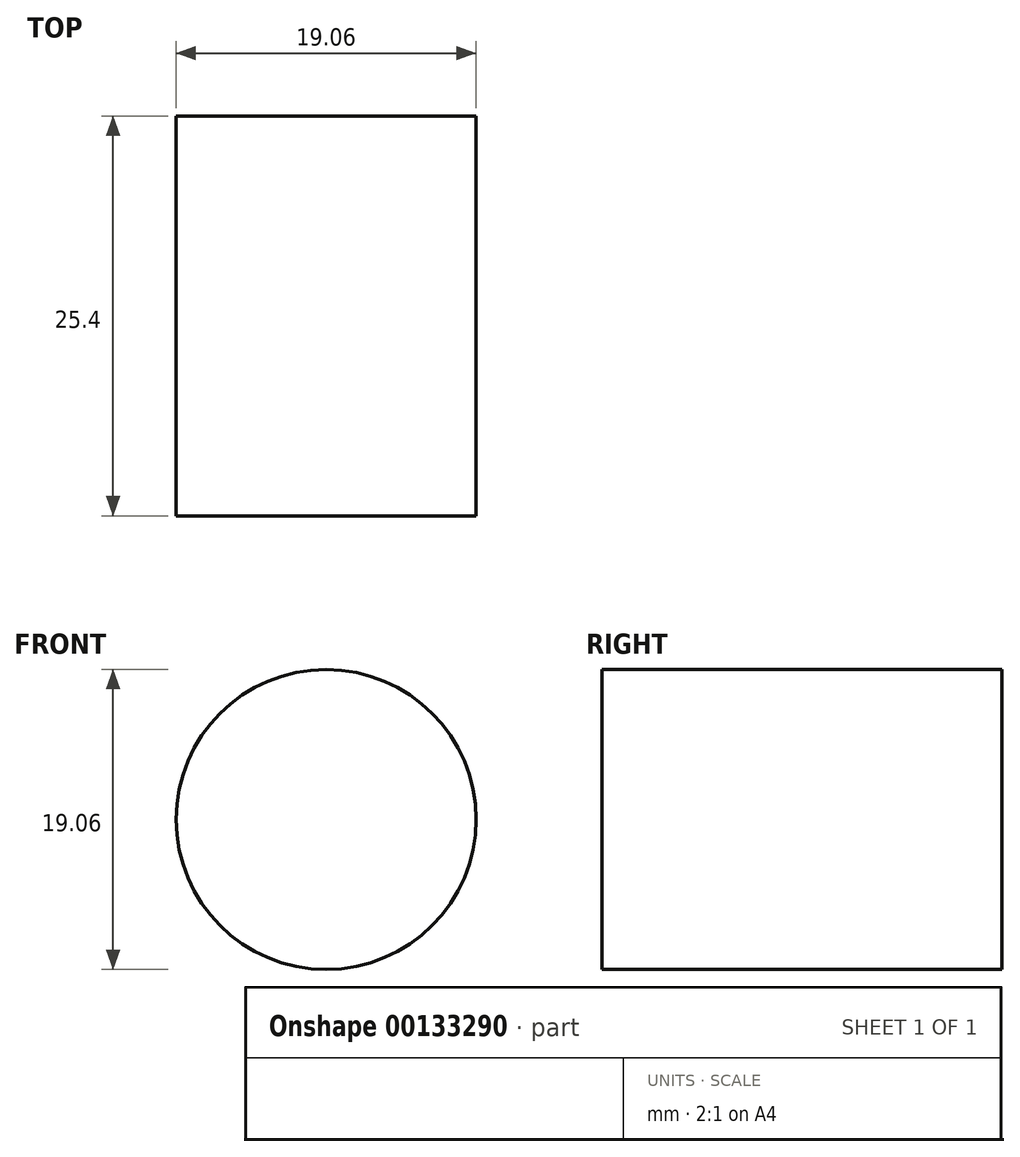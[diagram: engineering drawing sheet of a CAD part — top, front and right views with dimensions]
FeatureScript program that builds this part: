
annotation { "Feature Type Name" : "Feature", "Feature Type Description" : "" }
export const myFeature = defineFeature(function(context is Context, id is Id, definition is map)
    precondition{}
    {
        {
            var Q0;
            Q0=qCreatedBy(makeId("Front.planeOp"),FACE);
            var sketch = newSketch(context, id + "F0", { "sketchPlane" : qUnion([Q0])});
            skCircle(sketch, "E0", {"center": v(0, 0) * mm, "radius": 9.53 * mm});
            skSolve(sketch);
        }
        {
            var Q0;
            Q0 = qSketchRegion(id + "F0", true);
            extrude(context, id + "F1", {"entities" : qUnion([Q0]), "depth" : 25.4 * mm});
        }
        {
            var Q0;
            Q0=qCreatedBy(makeId("Front.planeOp"),FACE);
            var sketch = newSketch(context, id + "F2", { "sketchPlane" : qUnion([Q0])});
            skLineSegment(sketch, "E1.bottom", {"start": v(4.45, 4.45) * mm, "end": v(-4.45, 4.45) * mm});
            skLineSegment(sketch, "E1.top", {"start": v(4.45, -4.45) * mm, "end": v(-4.45, -4.45) * mm});
            skLineSegment(sketch, "E1.left", {"start": v(4.45, 4.45) * mm, "end": v(4.45, -4.45) * mm});
            skLineSegment(sketch, "E1.right", {"start": v(-4.45, 4.45) * mm, "end": v(-4.45, -4.45) * mm});
            skPoint(sketch, "E1.middle", {"position": v(0, 0) * mm});
            skCircle(sketch, "E2", {"center": v(0, 0) * mm, "radius": 4.45 * mm});
            skSolve(sketch);
        }
        {
            var Q0;
            Q0=sQuery(id+"F2.wireOp",EDGE,"E2");
            extrude(context, id + "F3", {"bodyType" : ToolBodyType.SURFACE, "surfaceEntities" : qUnion([Q0]), "endBound" : BoundingType.THROUGH_ALL, "depth" : 25.4 * mm});
        }
    });
